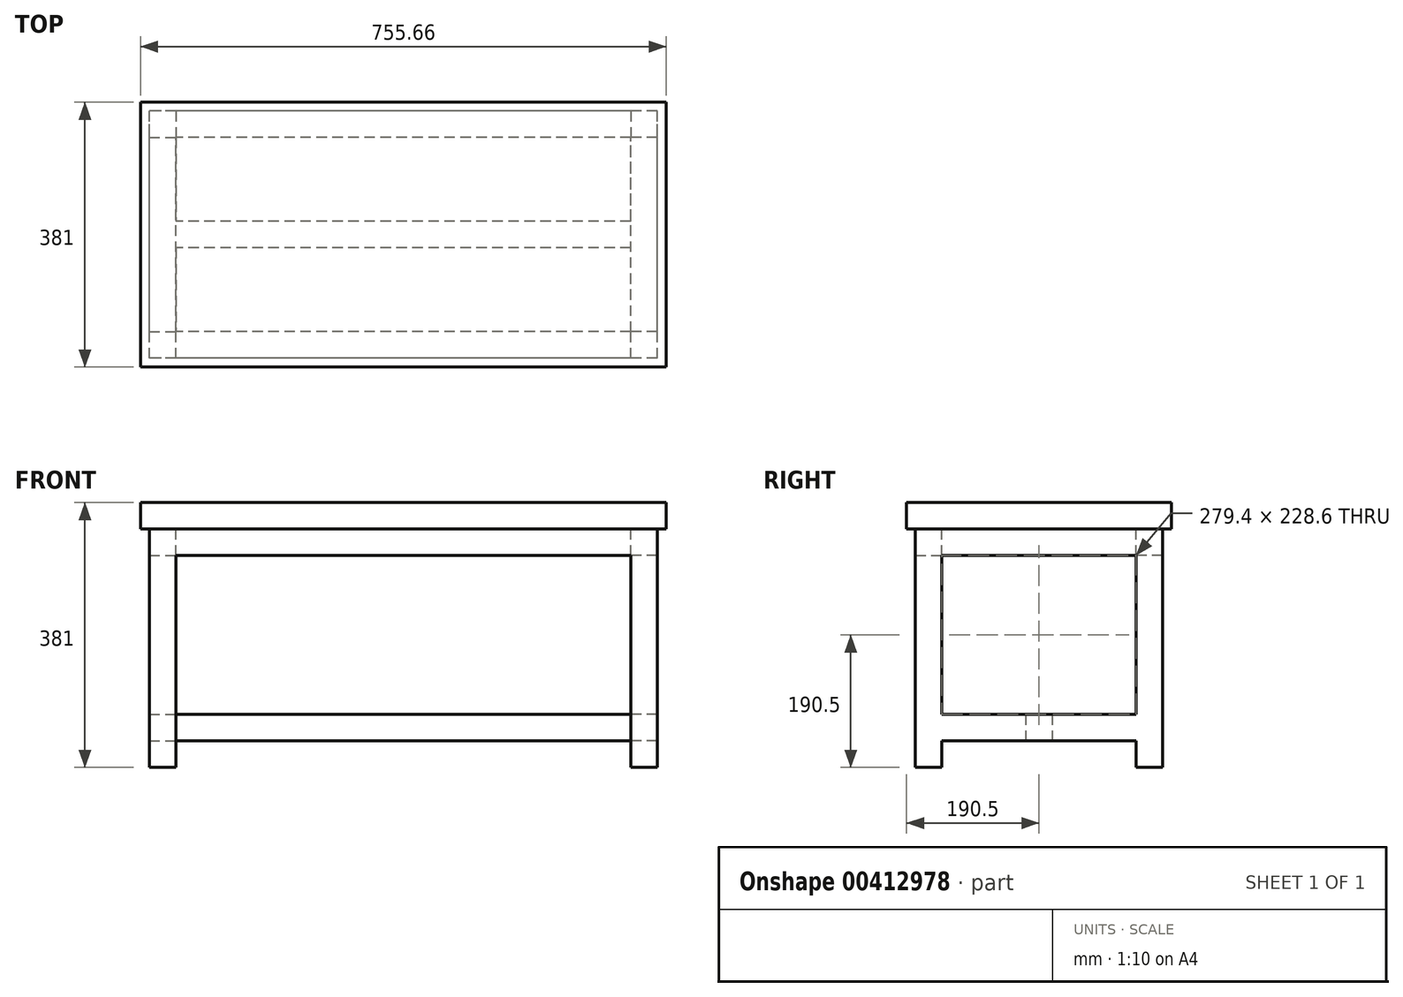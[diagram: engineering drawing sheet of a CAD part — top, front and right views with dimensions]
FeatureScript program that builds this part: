
annotation { "Feature Type Name" : "Feature", "Feature Type Description" : "" }
export const myFeature = defineFeature(function(context is Context, id is Id, definition is map)
    precondition{}
    {
        {
            var Q0;
            Q0=qCreatedBy(makeId("Top.planeOp"),FACE);
            var sketch = newSketch(context, id + "F0", { "sketchPlane" : qUnion([Q0])});
            skLineSegment(sketch, "E0.bottom", {"start": v(377.83, -190.5) * mm, "end": v(-377.83, -190.5) * mm});
            skLineSegment(sketch, "E0.top", {"start": v(377.83, 190.5) * mm, "end": v(-377.83, 190.5) * mm});
            skLineSegment(sketch, "E0.left", {"start": v(377.83, -190.5) * mm, "end": v(377.83, 190.5) * mm});
            skLineSegment(sketch, "E0.right", {"start": v(-377.83, -190.5) * mm, "end": v(-377.83, 190.5) * mm});
            skPoint(sketch, "E0.middle", {"position": v(0, 0) * mm});
            skSolve(sketch);
        }
        {
            var Q0;
            Q0 = qSketchRegion(id + "F0", true);
            extrude(context, id + "F1", {"entities" : qUnion([Q0]), "depth" : 38.1 * mm});
        }
        {
            var Q0;
            Q0=makeQuery(id+"F1.opExtrude","CAP_FACE",FACE,{"disambiguationData":[OSD([sQuery(id+"F0.wireOp",EDGE,"E0.bottom"),sQuery(id+"F0.wireOp",EDGE,"E0.top"),sQuery(id+"F0.wireOp",EDGE,"E0.left"),sQuery(id+"F0.wireOp",EDGE,"E0.right")])],"isStart":true});
            var sketch = newSketch(context, id + "F2", { "sketchPlane" : qUnion([Q0])});
            skLineSegment(sketch, "E1.0", {"start": v(365.13, 177.8) * mm, "end": v(-365.13, 177.8) * mm});
            skLineSegment(sketch, "E1.1", {"start": v(365.13, 177.8) * mm, "end": v(365.13, -177.8) * mm});
            skLineSegment(sketch, "E1.2", {"start": v(365.13, -177.8) * mm, "end": v(-365.13, -177.8) * mm});
            skLineSegment(sketch, "E1.3", {"start": v(-365.13, 177.8) * mm, "end": v(-365.13, -177.8) * mm});
            skLineSegment(sketch, "E2.0", {"start": v(327.03, 139.7) * mm, "end": v(-327.03, 139.7) * mm});
            skLineSegment(sketch, "E2.1", {"start": v(327.03, 139.7) * mm, "end": v(327.03, -139.7) * mm});
            skLineSegment(sketch, "E2.2", {"start": v(327.03, -139.7) * mm, "end": v(-327.03, -139.7) * mm});
            skLineSegment(sketch, "E2.3", {"start": v(-327.03, 139.7) * mm, "end": v(-327.03, -139.7) * mm});
            skLineSegment(sketch, "E3.0", {"start": v(371.48, -184.15) * mm, "end": v(371.48, 184.15) * mm, "construction": true});
            skLineSegment(sketch, "E3.1", {"start": v(-371.48, -184.15) * mm, "end": v(371.48, -184.15) * mm, "construction": true});
            skLineSegment(sketch, "E3.2", {"start": v(-371.48, 184.15) * mm, "end": v(-371.48, -184.15) * mm, "construction": true});
            skLineSegment(sketch, "E3.3", {"start": v(371.48, 184.15) * mm, "end": v(-371.48, 184.15) * mm, "construction": true});
            skSolve(sketch);
        }
        {
            var Q0;
            Q0 = qSketchRegion(id + "F2", true);
            extrude(context, id + "F3", {"entities" : qUnion([Q0]), "operationType" : NewBodyOperationType.ADD, "depth" : 38.1 * mm});
        }
        {
            var Q0;
            Q0=makeQuery(id+"F3.opExtrude","CAP_FACE",FACE,{"disambiguationData":[OSD([sQuery(id+"F2.wireOp",EDGE,"E1.0"),sQuery(id+"F2.wireOp",EDGE,"E1.1"),sQuery(id+"F2.wireOp",EDGE,"E1.2"),sQuery(id+"F2.wireOp",EDGE,"E1.3"),sQuery(id+"F2.wireOp",EDGE,"E2.0"),sQuery(id+"F2.wireOp",EDGE,"E2.1"),sQuery(id+"F2.wireOp",EDGE,"E2.2"),sQuery(id+"F2.wireOp",EDGE,"E2.3")])],"isStart":false});
            var sketch = newSketch(context, id + "F4", { "sketchPlane" : qUnion([Q0])});
            skLineSegment(sketch, "E4.bottom", {"start": v(-365.13, 177.8) * mm, "end": v(-327.03, 177.8) * mm});
            skLineSegment(sketch, "E4.top", {"start": v(-365.13, 139.7) * mm, "end": v(-327.03, 139.7) * mm});
            skLineSegment(sketch, "E4.left", {"start": v(-365.13, 177.8) * mm, "end": v(-365.13, 139.7) * mm});
            skLineSegment(sketch, "E4.right", {"start": v(-327.03, 177.8) * mm, "end": v(-327.03, 139.7) * mm});
            skLineSegment(sketch, "E5.bottom", {"start": v(365.13, 177.8) * mm, "end": v(327.03, 177.8) * mm});
            skLineSegment(sketch, "E5.top", {"start": v(365.13, 139.7) * mm, "end": v(327.03, 139.7) * mm});
            skLineSegment(sketch, "E5.left", {"start": v(365.13, 177.8) * mm, "end": v(365.13, 139.7) * mm});
            skLineSegment(sketch, "E5.right", {"start": v(327.03, 177.8) * mm, "end": v(327.03, 139.7) * mm});
            skLineSegment(sketch, "E6.bottom", {"start": v(365.13, -177.8) * mm, "end": v(327.03, -177.8) * mm});
            skLineSegment(sketch, "E6.top", {"start": v(365.13, -139.7) * mm, "end": v(327.03, -139.7) * mm});
            skLineSegment(sketch, "E6.left", {"start": v(365.13, -177.8) * mm, "end": v(365.13, -139.7) * mm});
            skLineSegment(sketch, "E6.right", {"start": v(327.03, -177.8) * mm, "end": v(327.03, -139.7) * mm});
            skLineSegment(sketch, "E7.bottom", {"start": v(-365.13, -177.8) * mm, "end": v(-327.03, -177.8) * mm});
            skLineSegment(sketch, "E7.top", {"start": v(-365.13, -139.7) * mm, "end": v(-327.03, -139.7) * mm});
            skLineSegment(sketch, "E7.left", {"start": v(-365.13, -177.8) * mm, "end": v(-365.13, -139.7) * mm});
            skLineSegment(sketch, "E7.right", {"start": v(-327.03, -177.8) * mm, "end": v(-327.03, -139.7) * mm});
            skSolve(sketch);
        }
        {
            var Q0;
            Q0 = qSketchRegion(id + "F4", true);
            extrude(context, id + "F5", {"entities" : qUnion([Q0]), "operationType" : NewBodyOperationType.ADD, "depth" : 304.8 * mm});
        }
        {
            var Q0;
            Q0=makeQuery(id+"F5.boolean.opBoolean","MERGE",FACE,{"derivedFrom":[makeQuery(id+"F3.opExtrude","SWEPT_FACE",FACE,{"disambiguationData":[OSD([sQuery(id+"F2.wireOp",EDGE,"E1.3")])]}),makeQuery(id+"F5.opExtrude","SWEPT_FACE",FACE,{"disambiguationData":[OSD([sQuery(id+"F4.wireOp",EDGE,"E4.left")])]}),makeQuery(id+"F5.opExtrude","SWEPT_FACE",FACE,{"disambiguationData":[OSD([sQuery(id+"F4.wireOp",EDGE,"E7.left")])]})]});
            var sketch = newSketch(context, id + "F6", { "sketchPlane" : qUnion([Q0])});
            skLineSegment(sketch, "E8.bottom", {"start": v(-177.8, -266.7) * mm, "end": v(177.8, -266.7) * mm});
            skLineSegment(sketch, "E8.top", {"start": v(-177.8, -304.8) * mm, "end": v(177.8, -304.8) * mm});
            skLineSegment(sketch, "E8.left", {"start": v(-177.8, -266.7) * mm, "end": v(-177.8, -304.8) * mm});
            skLineSegment(sketch, "E8.right", {"start": v(177.8, -266.7) * mm, "end": v(177.8, -304.8) * mm});
            skSolve(sketch);
        }
        {
            var Q0;
            Q0 = qSketchRegion(id + "F6", true);
            extrude(context, id + "F7", {"entities" : qUnion([Q0]), "operationType" : NewBodyOperationType.ADD, "oppositeDirection" : true, "depth" : 38.1 * mm});
        }
        {
            var Q0;
            Q0=makeQuery(id+"F5.boolean.opBoolean","MERGE",FACE,{"derivedFrom":[makeQuery(id+"F3.opExtrude","SWEPT_FACE",FACE,{"disambiguationData":[OSD([sQuery(id+"F2.wireOp",EDGE,"E1.1")])]}),makeQuery(id+"F5.opExtrude","SWEPT_FACE",FACE,{"disambiguationData":[OSD([sQuery(id+"F4.wireOp",EDGE,"E5.left")])]}),makeQuery(id+"F5.opExtrude","SWEPT_FACE",FACE,{"disambiguationData":[OSD([sQuery(id+"F4.wireOp",EDGE,"E6.left")])]})]});
            var sketch = newSketch(context, id + "F8", { "sketchPlane" : qUnion([Q0])});
            skLineSegment(sketch, "E9.bottom", {"start": v(-177.8, -266.7) * mm, "end": v(177.8, -266.7) * mm});
            skLineSegment(sketch, "E9.top", {"start": v(-177.8, -304.8) * mm, "end": v(177.8, -304.8) * mm});
            skLineSegment(sketch, "E9.left", {"start": v(-177.8, -266.7) * mm, "end": v(-177.8, -304.8) * mm});
            skLineSegment(sketch, "E9.right", {"start": v(177.8, -266.7) * mm, "end": v(177.8, -304.8) * mm});
            skSolve(sketch);
        }
        {
            var Q0;
            Q0 = qSketchRegion(id + "F8", true);
            extrude(context, id + "F9", {"entities" : qUnion([Q0]), "operationType" : NewBodyOperationType.ADD, "oppositeDirection" : true, "depth" : 38.1 * mm});
        }
        {
            var Q0;
            Q0=makeQuery(id+"F9.opExtrude","SWEPT_FACE",FACE,{"disambiguationData":[OSD([sQuery(id+"F8.wireOp",EDGE,"E9.top")])]});
            var sketch = newSketch(context, id + "F10", { "sketchPlane" : qUnion([Q0])});
            skLineSegment(sketch, "E10.bottom", {"start": v(365.13, -19.05) * mm, "end": v(-365.13, -19.05) * mm});
            skLineSegment(sketch, "E10.top", {"start": v(365.13, 19.05) * mm, "end": v(-365.13, 19.05) * mm});
            skLineSegment(sketch, "E10.left", {"start": v(365.13, -19.05) * mm, "end": v(365.13, 19.05) * mm});
            skLineSegment(sketch, "E10.right", {"start": v(-365.13, -19.05) * mm, "end": v(-365.13, 19.05) * mm});
            skLineSegment(sketch, "E11", {"start": v(365.13, 0) * mm, "end": v(-365.13, 0) * mm, "construction": true});
            skSolve(sketch);
        }
        {
            var Q0;
            Q0 = qSketchRegion(id + "F10", true);
            extrude(context, id + "F11", {"entities" : qUnion([Q0]), "operationType" : NewBodyOperationType.ADD, "oppositeDirection" : true, "depth" : 38.1 * mm});
        }
    });
